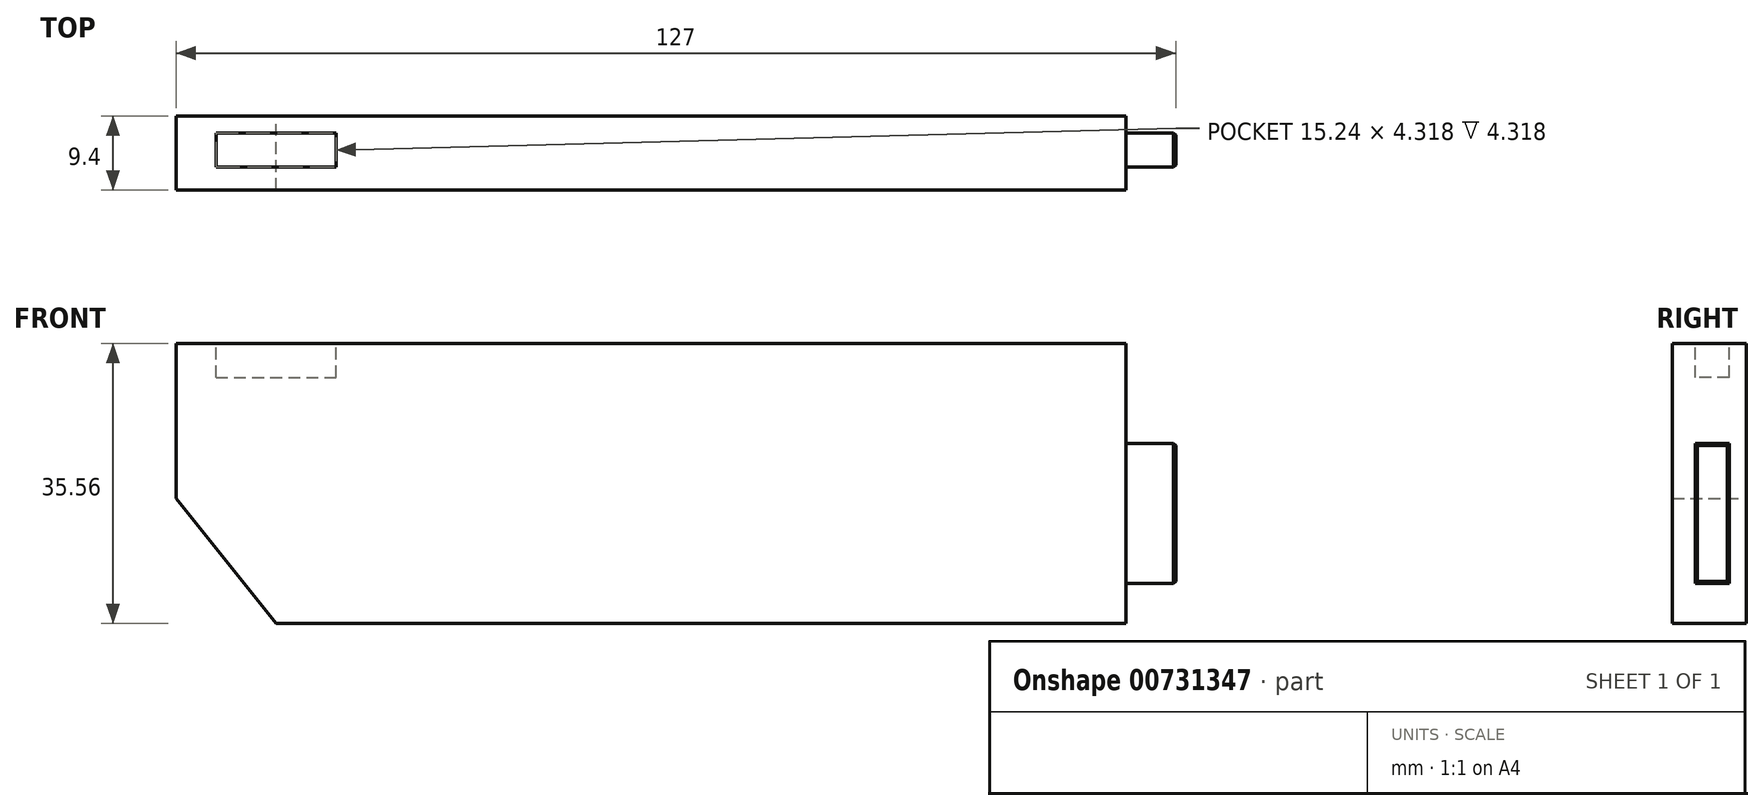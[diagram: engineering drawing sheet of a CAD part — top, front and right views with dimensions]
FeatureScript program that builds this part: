
annotation { "Feature Type Name" : "Feature", "Feature Type Description" : "" }
export const myFeature = defineFeature(function(context is Context, id is Id, definition is map)
    precondition{}
    {
        {
            var Q0;
            Q0=qCreatedBy(makeId("Front.planeOp"),FACE);
            var sketch = newSketch(context, id + "F0", { "sketchPlane" : qUnion([Q0])});
            skLineSegment(sketch, "E0", {"start": v(0, 0) * mm, "end": v(-120.65, 0) * mm});
            skLineSegment(sketch, "E1", {"start": v(0, 0) * mm, "end": v(0, -35.56) * mm});
            skLineSegment(sketch, "E2", {"start": v(0, -35.56) * mm, "end": v(-107.95, -35.56) * mm});
            skLineSegment(sketch, "E3", {"start": v(-107.95, -35.56) * mm, "end": v(-120.65, -19.7) * mm});
            skLineSegment(sketch, "E4", {"start": v(-120.65, -19.7) * mm, "end": v(-120.65, 0) * mm});
            skLineSegment(sketch, "E5", {"start": v(-120.65, -19.7) * mm, "end": v(-107.95, -19.7) * mm, "construction": true});
            skLineSegment(sketch, "E6", {"start": v(-6.98, 0) * mm, "end": v(-6.98, -10.16) * mm, "construction": true});
            skLineSegment(sketch, "E7", {"start": v(-6.98, -10.16) * mm, "end": v(-120.65, -10.16) * mm, "construction": true});
            skLineSegment(sketch, "E8", {"start": v(-107.95, -19.7) * mm, "end": v(-107.95, -35.56) * mm, "construction": true});
            skSolve(sketch);
        }
        {
            var Q0;
            Q0 = qSketchRegion(id + "F0", true);
            extrude(context, id + "F1", {"entities" : qUnion([Q0]), "depth" : 5.08 * mm, "offsetDistance" : 25.4 * mm, "hasSecondDirection" : true, "secondDirectionOppositeDirection" : true, "secondDirectionDepth" : 4.32 * mm});
        }
        {
            var Q0;
            Q0=makeQuery(id+"F1.opExtrude","SWEPT_FACE",FACE,{"disambiguationData":[OSD([sQuery(id+"F0.wireOp",EDGE,"E1")])]});
            var sketch = newSketch(context, id + "F2", { "sketchPlane" : qUnion([Q0])});
            skLineSegment(sketch, "E9.bottom", {"start": v(-2.16, -12.7) * mm, "end": v(2.16, -12.7) * mm});
            skLineSegment(sketch, "E10.top", {"start": v(-2.16, -30.48) * mm, "end": v(2.16, -30.48) * mm});
            skLineSegment(sketch, "E11", {"start": v(-2.16, -12.7) * mm, "end": v(-2.16, -30.48) * mm});
            skLineSegment(sketch, "E12", {"start": v(2.16, -12.7) * mm, "end": v(2.16, -30.48) * mm});
            skSolve(sketch);
        }
        {
            var Q0;
            Q0 = qSketchRegion(id + "F2", true);
            extrude(context, id + "F3", {"entities" : qUnion([Q0]), "operationType" : NewBodyOperationType.ADD, "depth" : 6.35 * mm, "offsetDistance" : 25.4 * mm});
        }
        {
            var Q0;
            Q0=makeQuery(id+"F1.opExtrude","SWEPT_FACE",FACE,{"disambiguationData":[OSD([sQuery(id+"F0.wireOp",EDGE,"E0")])]});
            var sketch = newSketch(context, id + "F4", { "sketchPlane" : qUnion([Q0])});
            skLineSegment(sketch, "E13.bottom", {"start": v(-115.57, 2.16) * mm, "end": v(-100.33, 2.16) * mm});
            skLineSegment(sketch, "E13.top", {"start": v(-115.57, -2.16) * mm, "end": v(-100.33, -2.16) * mm});
            skLineSegment(sketch, "E13.left", {"start": v(-115.57, 2.16) * mm, "end": v(-115.57, -2.16) * mm});
            skLineSegment(sketch, "E13.right", {"start": v(-100.33, 2.16) * mm, "end": v(-100.33, -2.16) * mm});
            skSolve(sketch);
        }
        {
            var Q0;
            Q0 = qSketchRegion(id + "F4", true);
            extrude(context, id + "F5", {"entities" : qUnion([Q0]), "operationType" : NewBodyOperationType.REMOVE, "oppositeDirection" : true, "depth" : 4.32 * mm, "offsetDistance" : 25.4 * mm});
        }
        {
            var Q0;
            Q0=makeQuery(id+"F3.opExtrude","CAP_FACE",FACE,{"disambiguationData":[OSD([sQuery(id+"F2.wireOp",EDGE,"E9.bottom"),sQuery(id+"F2.wireOp",EDGE,"E10.top"),sQuery(id+"F2.wireOp",EDGE,"E11"),sQuery(id+"F2.wireOp",EDGE,"E12")])],"isStart":false});
            chamfer(context, id + "F6", {"entities" : qUnion([Q0]), "width" : 0.25 * mm, "tangentPropagation" : true});
        }
    });
